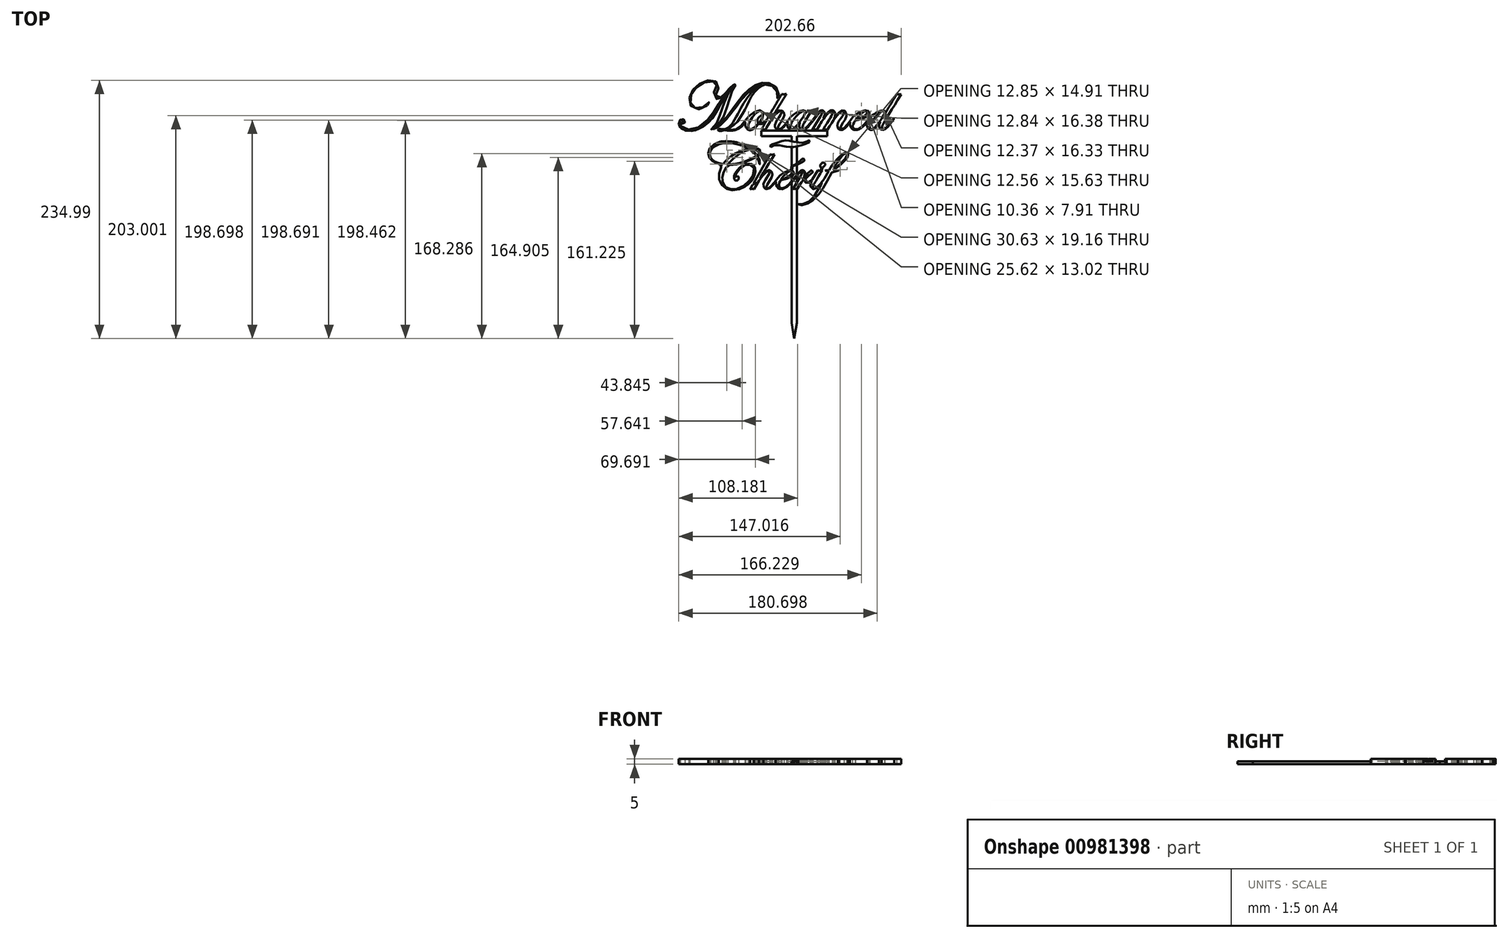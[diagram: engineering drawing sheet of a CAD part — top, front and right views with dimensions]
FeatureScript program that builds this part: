
annotation { "Feature Type Name" : "Feature", "Feature Type Description" : "" }
export const myFeature = defineFeature(function(context is Context, id is Id, definition is map)
    precondition{}
    {
        {
            var Q0;
            Q0=qCreatedBy(makeId("Top.planeOp"),FACE);
            var sketch = newSketch(context, id + "F0", { "sketchPlane" : qUnion([Q0])});
            skPoint(sketch, "E0", {"position": v(0, -6.46) * mm});
            skFitSpline(sketch, "E1", {"points": [v(-62.76, 39.27) * mm, v(-62.6, 39.54) * mm, v(-62.38, 39.63) * mm, v(-62.04, 39.52) * mm, v(-62, 38.94) * mm, v(-62.2, 38.46) * mm, v(-62.86, 37.49) * mm, v(-63.7, 36.53) * mm, v(-64.47, 35.77) * mm, v(-65.58, 34.8) * mm, v(-66.63, 34.03) * mm, v(-67.77, 33.57) * mm, v(-69, 33.44) * mm, v(-70.14, 33.54) * mm, v(-71.55, 34.27) * mm, v(-72.56, 35.4) * mm, v(-73.2, 36.81) * mm, v(-73.3, 38.17) * mm, v(-73.11, 39.6) * mm, v(-72.75, 40.63) * mm, v(-72.19, 41.92) * mm, v(-71.5, 43.34) * mm, v(-71.04, 44.4) * mm, v(-70.56, 45.74) * mm, v(-70.43, 46.6) * mm, v(-70.62, 47.57) * mm, v(-71.18, 48.46) * mm, v(-71.68, 48.93) * mm, v(-72.36, 49.32) * mm, v(-73.34, 49.67) * mm, v(-74.48, 49.91) * mm, v(-77.25, 49.95) * mm, v(-79.05, 49.67) * mm, v(-80.65, 49.25) * mm, v(-82.83, 48.34) * mm, v(-84.93, 47.23) * mm, v(-86.3, 46.3) * mm, v(-87.57, 45.33) * mm, v(-89.12, 43.96) * mm, v(-90.43, 42.65) * mm, v(-91.75, 41.08) * mm, v(-92.94, 39.15) * mm, v(-93.79, 37.48) * mm, v(-94.18, 36.2) * mm, v(-94.62, 34.55) * mm, v(-94.73, 33.03) * mm, v(-94.7, 31.33) * mm, v(-94.29, 29.7) * mm, v(-93.87, 28.77) * mm, v(-93.21, 27.84) * mm, v(-92.45, 26.95) * mm, v(-91.42, 26.19) * mm, v(-90.16, 25.63) * mm, v(-88.64, 25.3) * mm, v(-87.7, 25.27) * mm, v(-86.07, 25.4) * mm, v(-84.35, 25.84) * mm, v(-83.05, 26.37) * mm, v(-81.66, 27.15) * mm, v(-79.8, 28.44) * mm, v(-78.83, 29.35) * mm, v(-77.89, 30.4) * mm, v(-77.52, 30.98) * mm, v(-77.35, 31.17) * mm, v(-77.04, 31.24) * mm, v(-76.77, 31) * mm, v(-76.74, 30.42) * mm, v(-77.2, 29.8) * mm, v(-78.33, 28.66) * mm, v(-79.78, 27.44) * mm, v(-81.13, 26.47) * mm, v(-82.79, 25.55) * mm, v(-85.24, 24.7) * mm, v(-87.4, 24.46) * mm, v(-89.27, 24.57) * mm, v(-91.84, 25.48) * mm, v(-93.31, 26.58) * mm, v(-94.23, 27.62) * mm, v(-95, 28.9) * mm, v(-95.55, 30.89) * mm, v(-95.63, 32.2) * mm, v(-95.6, 33.98) * mm, v(-95.23, 35.93) * mm, v(-94.64, 37.86) * mm, v(-93.83, 39.46) * mm, v(-92.98, 40.93) * mm, v(-91.91, 42.4) * mm, v(-90.55, 43.9) * mm, v(-89.36, 45.03) * mm, v(-88.06, 46.14) * mm, v(-86.31, 47.4) * mm, v(-83.87, 48.82) * mm, v(-82.24, 49.54) * mm, v(-80.43, 50.12) * mm, v(-78.86, 50.5) * mm, v(-76.91, 50.72) * mm, v(-75.68, 50.77) * mm, v(-73.8, 50.66) * mm, v(-72.42, 50.28) * mm, v(-71.14, 49.63) * mm, v(-70.3, 48.91) * mm, v(-69.5, 47.8) * mm, v(-68.94, 46.44) * mm, v(-68.84, 44.6) * mm, v(-69.17, 42.94) * mm, v(-69.77, 41.1) * mm, v(-70.43, 39.66) * mm, v(-71, 38.32) * mm, v(-71.26, 37.62) * mm, v(-71.51, 36.56) * mm, v(-71.42, 35.54) * mm, v(-70.69, 34.74) * mm, v(-69.92, 34.4) * mm, v(-68.4, 34.37) * mm, v(-66.52, 35.2) * mm, v(-64.51, 36.88) * mm, v(-63.27, 38.48) * mm, v(-62.76, 39.27) * mm]});
            skFitSpline(sketch, "E2", {"points": [v(-104.1, 12.23) * mm, v(-104.04, 12.78) * mm, v(-103.88, 13.03) * mm, v(-103.68, 13.06) * mm, v(-103.53, 12.82) * mm, v(-103.51, 12.13) * mm, v(-103.41, 11.53) * mm, v(-103, 11.02) * mm, v(-102.14, 10.75) * mm, v(-101.11, 10.84) * mm, v(-100.18, 11.53) * mm, v(-99.66, 12.4) * mm, v(-99.52, 13.2) * mm, v(-99.6, 14.3) * mm, v(-100.24, 15.07) * mm, v(-101.15, 15.48) * mm, v(-102.26, 15.45) * mm, v(-103.07, 15.2) * mm, v(-103.62, 14.87) * mm, v(-104.24, 14.22) * mm, v(-104.8, 13.28) * mm, v(-105.02, 12.5) * mm, v(-105.16, 11.06) * mm, v(-104.76, 9.4) * mm, v(-104.06, 8.18) * mm, v(-102.92, 7.05) * mm, v(-101.64, 6.2) * mm, v(-100.35, 5.54) * mm, v(-98.95, 5.08) * mm, v(-97.71, 4.81) * mm, v(-95.52, 4.68) * mm, v(-93.28, 4.78) * mm, v(-90.97, 5.17) * mm, v(-88.23, 5.96) * mm, v(-85.63, 7.09) * mm, v(-83.84, 8.17) * mm, v(-81.5, 9.62) * mm, v(-79.45, 11.14) * mm, v(-78.05, 12.46) * mm, v(-76.34, 14.26) * mm, v(-75.31, 15.46) * mm, v(-73.29, 18.2) * mm, v(-71.17, 21.5) * mm, v(-69.94, 23.64) * mm, v(-68.77, 25.81) * mm, v(-67.45, 28.3) * mm, v(-66.25, 30.54) * mm, v(-65.24, 32.46) * mm, v(-64.39, 33.83) * mm, v(-63.74, 34.91) * mm, v(-61.65, 38.33) * mm, v(-60.27, 40.28) * mm, v(-58.56, 42.43) * mm, v(-57.54, 43.6) * mm, v(-56.65, 44.53) * mm, v(-55.73, 45.31) * mm, v(-55.47, 45.4) * mm, v(-55.9, 44.92) * mm, v(-56.63, 44.19) * mm, v(-57.73, 42.77) * mm, v(-58.66, 41.39) * mm, v(-59.5, 39.98) * mm, v(-60.38, 38.35) * mm, v(-61.43, 36.24) * mm, v(-62.16, 34.56) * mm, v(-62.9, 32.68) * mm, v(-64.37, 28.71) * mm, v(-65.1, 26.41) * mm, v(-67.48, 19.6) * mm, v(-67.94, 18.27) * mm, v(-68.34, 17.02) * mm, v(-68.94, 15.55) * mm, v(-69.85, 13.29) * mm, v(-70.55, 11.74) * mm, v(-71.24, 10.5) * mm, v(-72.42, 8.82) * mm, v(-73.72, 7.5) * mm, v(-74.86, 6.53) * mm, v(-75.6, 5.98) * mm, v(-75.99, 5.56) * mm, v(-75.66, 5.35) * mm, v(-74.58, 5.5) * mm, v(-72.84, 6.15) * mm, v(-71.4, 6.88) * mm, v(-69.46, 8.15) * mm, v(-67.86, 9.28) * mm, v(-66.16, 10.88) * mm, v(-62.54, 14.6) * mm, v(-57.85, 20.25) * mm, v(-54.53, 24.54) * mm, v(-48.39, 32.59) * mm, v(-46.3, 35.03) * mm, v(-44.15, 37.45) * mm, v(-41.9, 39.66) * mm, v(-40.15, 41.13) * mm, v(-38, 42.77) * mm, v(-36.35, 43.94) * mm, v(-34.71, 44.81) * mm, v(-32.96, 45.7) * mm, v(-31.49, 46.26) * mm, v(-29.49, 46.72) * mm, v(-27.83, 46.97) * mm, v(-25.56, 46.97) * mm, v(-23.7, 46.76) * mm, v(-22, 46.36) * mm, v(-20.3, 45.61) * mm, v(-18.65, 44.49) * mm, v(-17.22, 43.17) * mm, v(-16.1, 41.57) * mm, v(-15.4, 39.99) * mm, v(-15.07, 37.97) * mm, v(-15.1, 36.15) * mm, v(-15.4, 34.86) * mm, v(-15.56, 34.23) * mm, v(-15.34, 33.85) * mm, v(-14.82, 33.98) * mm, v(-14.52, 34.86) * mm, v(-14.17, 36.97) * mm, v(-14.3, 39.57) * mm, v(-15.1, 42.09) * mm, v(-15.93, 43.6) * mm, v(-17.45, 45.29) * mm, v(-19.53, 46.83) * mm, v(-20.68, 47.48) * mm, v(-23.27, 48.27) * mm, v(-24.66, 48.44) * mm, v(-26.15, 48.51) * mm, v(-27.8, 48.5) * mm, v(-29.22, 48.3) * mm, v(-31.25, 47.89) * mm, v(-33.64, 47.08) * mm, v(-35.38, 46.28) * mm, v(-36.97, 45.39) * mm, v(-38.48, 44.45) * mm, v(-40.35, 43.04) * mm, v(-41.41, 42.23) * mm, v(-43.69, 40.18) * mm, v(-45.56, 38.24) * mm, v(-46.75, 36.95) * mm, v(-49.15, 33.96) * mm, v(-50.8, 31.9) * mm, v(-52.5, 29.6) * mm, v(-53.49, 28.19) * mm, v(-55.27, 25.76) * mm, v(-57.05, 23.37) * mm, v(-59.03, 20.64) * mm, v(-60.43, 18.83) * mm, v(-63.08, 15.44) * mm, v(-65.51, 12.66) * mm, v(-66.88, 11.3) * mm, v(-68.94, 9.66) * mm, v(-71.06, 7.98) * mm, v(-72.8, 7.01) * mm, v(-73.58, 6.72) * mm, v(-71.93, 7.85) * mm, v(-70.57, 8.92) * mm, v(-68.96, 10.5) * mm, v(-67.4, 12.3) * mm, v(-66.06, 14.46) * mm, v(-65.1, 16.1) * mm, v(-63.36, 20.12) * mm, v(-62.63, 22.2) * mm, v(-61.07, 26.75) * mm, v(-60.4, 28.98) * mm, v(-59.35, 32.54) * mm, v(-58.7, 34.84) * mm, v(-57.69, 38.18) * mm, v(-56.82, 40.68) * mm, v(-55.97, 42.75) * mm, v(-55.12, 44.3) * mm, v(-54.29, 45.57) * mm, v(-53.7, 46.31) * mm, v(-53.58, 46.76) * mm, v(-53.87, 46.94) * mm, v(-54.62, 46.82) * mm, v(-55.46, 46.4) * mm, v(-56.39, 45.69) * mm, v(-57.57, 44.61) * mm, v(-58.95, 43.18) * mm, v(-60.16, 41.84) * mm, v(-61.62, 40) * mm, v(-62.7, 38.53) * mm, v(-63.62, 37.28) * mm, v(-66.11, 33.26) * mm, v(-68.3, 29.8) * mm, v(-70.88, 25.5) * mm, v(-74, 20.58) * mm, v(-76, 17.9) * mm, v(-78.55, 15.03) * mm, v(-81.03, 12.4) * mm, v(-83.53, 10.18) * mm, v(-86.75, 8.1) * mm, v(-88.75, 7.17) * mm, v(-91.29, 6.27) * mm, v(-93.65, 5.83) * mm, v(-95.92, 5.76) * mm, v(-98.1, 6.06) * mm, v(-100.25, 6.67) * mm, v(-101.85, 7.59) * mm, v(-103.04, 8.67) * mm, v(-103.93, 10.37) * mm, v(-104.1, 12.23) * mm]});
            skFitSpline(sketch, "E3", {"points": [v(-63.32, 5.52) * mm, v(-66.2, 4.77) * mm, v(-68.7, 4.84) * mm, v(-69.35, 5.3) * mm, v(-69.4, 5.82) * mm, v(-68.9, 6.32) * mm, v(-67.94, 6.54) * mm, v(-66.1, 6.52) * mm, v(-63.68, 6.27) * mm, v(-62.84, 6.32) * mm, v(-60.23, 7.8) * mm, v(-58.78, 8.88) * mm, v(-57.03, 10.78) * mm, v(-55.7, 12.64) * mm, v(-54.18, 15.1) * mm, v(-52.3, 18.5) * mm, v(-50.64, 21.58) * mm, v(-49, 24.67) * mm, v(-47.62, 27.12) * mm, v(-46.44, 29.09) * mm, v(-45.4, 30.83) * mm, v(-44.24, 32.7) * mm, v(-43.1, 34.35) * mm, v(-41.72, 36.3) * mm, v(-39.95, 38.46) * mm, v(-38, 40.5) * mm, v(-36.26, 42.08) * mm, v(-34.22, 43.79) * mm, v(-32.29, 45.03) * mm, v(-30.12, 46.32) * mm, v(-28.34, 47.09) * mm, v(-27.84, 47.24) * mm, v(-27.52, 47.28) * mm, v(-27.04, 47.35) * mm, v(-26.54, 47.2) * mm, v(-26.48, 46.92) * mm, v(-27.17, 46.74) * mm, v(-28.2, 46.4) * mm, v(-28.76, 46.13) * mm, v(-29.34, 45.78) * mm, v(-30, 45.37) * mm, v(-30.62, 45.06) * mm, v(-31.68, 44.34) * mm, v(-32.7, 43.6) * mm, v(-33.44, 43.04) * mm, v(-34.4, 42.08) * mm, v(-35.77, 40.67) * mm, v(-36.94, 39.15) * mm, v(-37.87, 37.68) * mm, v(-38.6, 36.5) * mm, v(-39.2, 35.42) * mm, v(-39.79, 34.5) * mm, v(-40.19, 33.77) * mm, v(-40.75, 32.7) * mm, v(-41.26, 31.67) * mm, v(-41.62, 31) * mm, v(-42.18, 29.78) * mm, v(-42.92, 28.27) * mm, v(-43.45, 27.13) * mm, v(-44.15, 25.75) * mm, v(-44.62, 24.83) * mm, v(-44.97, 24.09) * mm, v(-45.53, 23.05) * mm, v(-46.17, 21.85) * mm, v(-46.75, 20.78) * mm, v(-47.21, 19.95) * mm, v(-47.82, 18.93) * mm, v(-48.34, 18.04) * mm, v(-48.88, 17.13) * mm, v(-49.57, 16.14) * mm, v(-50.23, 15.23) * mm, v(-50.98, 14.15) * mm, v(-51.55, 13.43) * mm, v(-52.25, 12.58) * mm, v(-53.48, 11.3) * mm, v(-54.25, 10.55) * mm, v(-55.18, 9.76) * mm, v(-55.99, 9.09) * mm, v(-56.92, 8.44) * mm, v(-58.17, 7.68) * mm, v(-59.45, 6.97) * mm, v(-60.42, 6.48) * mm, v(-61.18, 6.2) * mm, v(-61.82, 5.97) * mm, v(-61.76, 5.87) * mm, v(-61.43, 5.86) * mm, v(-61.16, 5.82) * mm, v(-60.3, 5.74) * mm, v(-58.93, 5.64) * mm, v(-57.24, 5.68) * mm, v(-55.93, 5.81) * mm, v(-54.73, 6) * mm, v(-53.3, 6.36) * mm, v(-51.67, 6.97) * mm, v(-49.92, 8.03) * mm, v(-48.15, 9.83) * mm, v(-46.49, 11.62) * mm, v(-44.96, 13.52) * mm, v(-43.55, 15.23) * mm, v(-42.2, 16.92) * mm, v(-41.29, 17.9) * mm, v(-40, 19.03) * mm, v(-37.87, 20.7) * mm, v(-36.32, 21.7) * mm, v(-34.55, 22.63) * mm, v(-33.29, 23.08) * mm, v(-31.7, 23.43) * mm, v(-30.46, 23.43) * mm, v(-29.44, 23.19) * mm, v(-28.5, 22.42) * mm, v(-28.03, 20.64) * mm, v(-28.19, 19.02) * mm, v(-28.68, 17.2) * mm, v(-29.05, 16.3) * mm, v(-30.17, 14.18) * mm, v(-31.1, 12.8) * mm, v(-31.9, 11.8) * mm], "startDerivative": vector(-226.38, -73.79) * mm, "endDerivative": vector(-96.8, -119.92) * mm});
            skFitSpline(sketch, "E4", {"points": [v(-31.9, 11.8) * mm, v(-31.47, 11.66) * mm, v(-30.7, 11.57) * mm, v(-29.75, 11.67) * mm, v(-28.23, 12.3) * mm, v(-27.16, 13.03) * mm, v(-25.9, 14.1) * mm, v(-24.7, 15.46) * mm, v(-24.13, 16.4) * mm, v(-23.54, 17.52) * mm, v(-22.98, 18.48) * mm, v(-22.43, 19.48) * mm], "startDerivative": vector(6.79, -2.6) * mm, "endDerivative": vector(6.08, 11.27) * mm});
            skFitSpline(sketch, "E5", {"points": [v(-22.43, 19.48) * mm, v(-21.36, 21.31) * mm, v(-20.4, 22.93) * mm, v(-19.52, 24.34) * mm, v(-18.1, 26.8) * mm, v(-17.02, 28.68) * mm, v(-15.7, 30.88) * mm, v(-15.2, 31.72) * mm, v(-13.65, 34.35) * mm, v(-13.2, 35.13) * mm, v(-12.36, 36.53) * mm, v(-11.9, 37.3) * mm, v(-11.26, 38.29) * mm], "startDerivative": vector(11.81, 20.1) * mm, "endDerivative": vector(10.2, 15.26) * mm});
            skFitSpline(sketch, "E6", {"points": [v(-11.26, 38.29) * mm, v(-10.67, 38.12) * mm, v(-9.9, 38.03) * mm, v(-8.89, 38.09) * mm, v(-8, 38.26) * mm, v(-7.1, 38.43) * mm], "startDerivative": vector(3.35, -1.1) * mm, "endDerivative": vector(4.37, 0.78) * mm});
            skFitSpline(sketch, "E7", {"points": [v(-7.1, 38.43) * mm, v(-7.44, 37.63) * mm, v(-8.1, 36.6) * mm, v(-8.92, 35.3) * mm, v(-9.6, 34.17) * mm, v(-10.49, 32.76) * mm, v(-11.34, 31.36) * mm, v(-12.43, 29.63) * mm, v(-13.38, 28.14) * mm, v(-14.27, 26.65) * mm, v(-15.73, 24.38) * mm, v(-17.3, 21.75) * mm, v(-18.56, 19.73) * mm, v(-19.17, 18.74) * mm, v(-19.9, 17.58) * mm, v(-21.04, 15.8) * mm], "startDerivative": vector(-6.48, -16.6) * mm, "endDerivative": vector(-16.06, -25.3) * mm});
            skFitSpline(sketch, "E8", {"points": [v(-21.04, 15.8) * mm, v(-18.36, 19.32) * mm, v(-17.41, 20.38) * mm, v(-16.07, 21.7) * mm, v(-14.6, 22.74) * mm, v(-13.55, 23.26) * mm, v(-12.65, 23.4) * mm, v(-11.95, 23.34) * mm, v(-10.76, 22.9) * mm, v(-10.02, 22.09) * mm, v(-9.52, 21.36) * mm, v(-9.21, 20.47) * mm, v(-9.1, 19.25) * mm, v(-9.12, 18.51) * mm, v(-9.49, 17.44) * mm, v(-10.14, 15.99) * mm, v(-10.81, 14.7) * mm, v(-11.79, 13.24) * mm, v(-12.6, 11.98) * mm, v(-13.14, 11.18) * mm, v(-13.7, 10.2) * mm, v(-14.4, 9.01) * mm, v(-14.85, 8.02) * mm, v(-14.97, 7.4) * mm, v(-14.9, 6.92) * mm, v(-14.62, 6.52) * mm, v(-14.16, 6.28) * mm, v(-13.77, 6.22) * mm, v(-13.27, 6.26) * mm, v(-12.64, 6.58) * mm, v(-11.64, 7.27) * mm, v(-10.4, 8.35) * mm, v(-8.9, 10.02) * mm, v(-7.64, 11.56) * mm, v(-6.53, 13.01) * mm, v(-5.44, 14.45) * mm, v(-4.64, 15.68) * mm, v(-3.7, 16.85) * mm, v(-2.77, 17.87) * mm, v(-1.7, 18.82) * mm, v(0.13, 20.1) * mm, v(1.71, 21.07) * mm, v(3.69, 22.1) * mm, v(5.9, 23.02) * mm, v(7.26, 23.32) * mm, v(8.27, 23.41) * mm, v(9, 23.37) * mm, v(9.8, 23) * mm, v(10.2, 22.5) * mm, v(10.34, 21.54) * mm, v(10.22, 20.53) * mm], "startDerivative": vector(80.75, 108.83) * mm, "endDerivative": vector(-9.77, -54.96) * mm});
            skFitSpline(sketch, "E9", {"points": [v(10.22, 20.53) * mm, v(11.54, 23.23) * mm], "startDerivative": vector(1.32, 2.7) * mm, "endDerivative": vector(1.32, 2.7) * mm});
            skFitSpline(sketch, "E10", {"points": [v(11.54, 23.23) * mm, v(12.61, 22.99) * mm, v(13.89, 22.94) * mm, v(15.2, 23.13) * mm, v(15.66, 23.23) * mm], "startDerivative": vector(4.04, -1.07) * mm, "endDerivative": vector(2.28, 0.55) * mm});
            skFitSpline(sketch, "E11", {"points": [v(15.66, 23.23) * mm, v(10.54, 14.73) * mm, v(8.84, 11.8) * mm, v(7.99, 10.1) * mm, v(7.41, 8.81) * mm, v(7.14, 7.7) * mm, v(7.22, 6.93) * mm, v(7.6, 6.39) * mm, v(8.26, 6.17) * mm, v(8.96, 6.4) * mm, v(10.1, 7.1) * mm, v(11.54, 8.33) * mm, v(12.8, 9.7) * mm, v(14.4, 11.54) * mm, v(16.4, 14.14) * mm, v(19.12, 17.77) * mm, v(21.84, 21.16) * mm, v(23.21, 22.42) * mm, v(24.17, 23.11) * mm, v(24.91, 23.34) * mm, v(25.41, 23.37) * mm, v(26.06, 23.23) * mm, v(26.68, 22.75) * mm, v(27.26, 22.03) * mm, v(27.58, 21.16) * mm, v(27.68, 19.72) * mm, v(27.5, 18.75) * mm, v(27.1, 17.5) * mm, v(26.56, 16.41) * mm], "startDerivative": vector(-65.23, -108.07) * mm, "endDerivative": vector(-18.62, -33.73) * mm});
            skFitSpline(sketch, "E12", {"points": [v(26.56, 16.41) * mm, v(28.85, 19.48) * mm, v(30.36, 21.14) * mm, v(31.88, 22.56) * mm, v(32.93, 23.17) * mm, v(34, 23.47) * mm, v(34.57, 23.44) * mm, v(35, 23.31) * mm, v(35.64, 23) * mm, v(36.2, 22.53) * mm, v(36.59, 22.01) * mm, v(36.9, 21.41) * mm, v(37.21, 20.46) * mm, v(37.24, 19.54) * mm, v(37.19, 18.78) * mm, v(36.9, 17.76) * mm, v(36.57, 17) * mm, v(36.38, 16.64) * mm, v(35.97, 15.93) * mm], "startDerivative": vector(22.24, 30.87) * mm, "endDerivative": vector(-9.01, -15.88) * mm});
            skFitSpline(sketch, "E13", {"points": [v(35.97, 15.93) * mm, v(36.82, 17.06) * mm, v(37.6, 18.08) * mm, v(39.05, 19.83) * mm, v(39.96, 20.74) * mm, v(40.85, 21.59) * mm, v(41.7, 22.3) * mm, v(42.6, 22.9) * mm, v(43.55, 23.33) * mm, v(44.26, 23.45) * mm, v(45.03, 23.37) * mm, v(45.86, 23) * mm, v(46.26, 22.72) * mm, v(46.7, 22.26) * mm, v(47.05, 21.73) * mm, v(47.4, 20.94) * mm, v(47.6, 20.08) * mm, v(47.66, 18.94) * mm, v(47.56, 18.15) * mm, v(47.17, 16.86) * mm, v(46.6, 15.56) * mm, v(45.96, 14.48) * mm, v(45.4, 13.66) * mm, v(44.74, 12.7) * mm, v(43.72, 11.2) * mm, v(42.76, 9.7) * mm, v(42.12, 8.38) * mm, v(41.94, 7.4) * mm, v(42.07, 6.72) * mm, v(42.5, 6.32) * mm, v(43, 6.2) * mm, v(43.97, 6.39) * mm, v(45.43, 7.39) * mm, v(46.87, 8.84) * mm, v(48.7, 10.9) * mm, v(50.37, 13.12) * mm, v(51.63, 14.79) * mm, v(51.99, 15.46) * mm, v(53.4, 17.3) * mm, v(54.66, 18.5) * mm, v(57, 20.22) * mm, v(59.17, 21.44) * mm, v(60.84, 22.29) * mm, v(62.37, 22.89) * mm, v(64, 23.32) * mm, v(65.06, 23.44) * mm, v(66.04, 23.34) * mm, v(67, 22.97) * mm, v(67.58, 22.51) * mm, v(68, 21.93) * mm, v(68.23, 21.06) * mm, v(68.12, 20.02) * mm, v(67.6, 18.97) * mm, v(66.85, 18.2) * mm, v(65.47, 17.2) * mm, v(64.43, 16.66) * mm, v(62.97, 16.06) * mm, v(61.16, 15.45) * mm, v(59.33, 14.96) * mm, v(57.58, 14.53) * mm, v(56.16, 14.23) * mm, v(55.4, 14.1) * mm], "startDerivative": vector(50.94, 68.1) * mm, "endDerivative": vector(-55.23, -9.52) * mm});
            skFitSpline(sketch, "E14", {"points": [v(55.91, 14.87) * mm, v(57.46, 16.93) * mm, v(58.45, 18.06) * mm, v(60.25, 19.86) * mm, v(61.8, 21.2) * mm, v(63.51, 22.28) * mm, v(64.8, 22.7) * mm, v(65.3, 22.74) * mm, v(65.75, 22.7) * mm, v(66, 22.54) * mm, v(66.14, 22.35) * mm, v(66.23, 22.11) * mm, v(66.26, 21.75) * mm, v(66.13, 21.22) * mm, v(65.85, 20.61) * mm, v(65.31, 19.87) * mm, v(64.48, 19) * mm, v(63.86, 18.5) * mm, v(62.89, 17.82) * mm, v(61.56, 17.03) * mm, v(60.34, 16.41) * mm, v(59.28, 15.98) * mm, v(58.2, 15.56) * mm, v(56.87, 15.12) * mm, v(56.13, 14.9) * mm], "startDerivative": vector(24.92, 34) * mm, "endDerivative": vector(-18.62, -5.6) * mm});
            skLineSegment(sketch, "E15", {"start": v(56.13, 14.9) * mm, "end": v(55.89, 14.83) * mm});
            skLineSegment(sketch, "E16", {"start": v(55.89, 14.83) * mm, "end": v(55.91, 14.87) * mm});
            skFitSpline(sketch, "E17", {"points": [v(55.4, 14.1) * mm, v(54.5, 12.55) * mm, v(53.8, 11.05) * mm, v(53.52, 10.15) * mm, v(53.34, 8.86) * mm, v(53.46, 7.97) * mm, v(53.84, 7.13) * mm, v(54.73, 6.5) * mm, v(55.79, 6.29) * mm, v(57.03, 6.34) * mm, v(58.73, 6.87) * mm, v(60.3, 7.77) * mm, v(62.03, 9.06) * mm, v(63.07, 9.99) * mm, v(65.78, 12.97) * mm, v(67.24, 14.7) * mm, v(68.42, 16.26) * mm, v(69.25, 17.23) * mm, v(70.65, 18.53) * mm, v(72.06, 19.61) * mm, v(73.72, 20.7) * mm, v(75.22, 21.56) * mm, v(77.15, 22.53) * mm, v(78.93, 23.16) * mm, v(80.73, 23.44) * mm, v(81.81, 23.26) * mm, v(82.54, 22.72) * mm, v(82.86, 21.82) * mm, v(82.77, 20.74) * mm, v(82.49, 20.05) * mm], "startDerivative": vector(-24.88, -40.4) * mm, "endDerivative": vector(-13.28, -26.18) * mm});
            skFitSpline(sketch, "E18", {"points": [v(82.49, 20.05) * mm, v(84.14, 22.87) * mm, v(86.37, 26.76) * mm, v(87.98, 29.35) * mm, v(89.95, 32.64) * mm, v(91.24, 34.84) * mm, v(93.3, 38.26) * mm], "startDerivative": vector(9.7, 16.4) * mm, "endDerivative": vector(12.45, 20.61) * mm});
            skFitSpline(sketch, "E19", {"points": [v(93.3, 38.26) * mm, v(93.92, 38.1) * mm, v(94.92, 37.9) * mm, v(96.11, 37.91) * mm, v(97.5, 38.1) * mm], "startDerivative": vector(3, -0.71) * mm, "endDerivative": vector(4.41, 0.64) * mm});
            skFitSpline(sketch, "E20", {"points": [v(97.5, 38.1) * mm, v(93.97, 32.48) * mm, v(92.6, 30.28) * mm, v(90.43, 26.74) * mm, v(88.7, 23.97) * mm, v(86.24, 19.97) * mm, v(84.77, 17.56) * mm, v(83.26, 15.14) * mm, v(81.73, 12.49) * mm, v(80.79, 10.64) * mm, v(79.88, 8.77) * mm, v(79.64, 7.97) * mm, v(79.6, 7.38) * mm, v(79.71, 6.8) * mm, v(80.03, 6.45) * mm, v(80.53, 6.22) * mm, v(80.96, 6.2) * mm, v(81.71, 6.46) * mm, v(82.92, 7.22) * mm, v(84.12, 8.27) * mm, v(84.81, 8.94) * mm, v(86.15, 10.5) * mm, v(87.22, 11.82) * mm, v(88.64, 13.73) * mm, v(89.42, 14.81) * mm, v(90.33, 16.14) * mm, v(90.54, 16.4) * mm, v(90.79, 16.46) * mm, v(90.97, 16.4) * mm, v(91.05, 16.15) * mm, v(90.93, 15.82) * mm, v(90.58, 15.3) * mm, v(90.15, 14.73) * mm, v(89.4, 13.64) * mm, v(88.6, 12.63) * mm, v(87.4, 11.08) * mm, v(86.51, 9.97) * mm, v(85.05, 8.31) * mm, v(84.26, 7.55) * mm, v(83.3, 6.74) * mm, v(82.42, 6.11) * mm, v(81.6, 5.66) * mm, v(80.82, 5.47) * mm, v(80.06, 5.5) * mm, v(79.32, 5.68) * mm, v(78.51, 6.14) * mm, v(77.89, 6.84) * mm, v(77.42, 7.78) * mm, v(77.27, 8.65) * mm, v(77.18, 9.4) * mm, v(77.3, 10.64) * mm, v(77.58, 11.55) * mm, v(77.88, 12.33) * mm, v(78.2, 12.94) * mm], "startDerivative": vector(-93.17, -148.36) * mm, "endDerivative": vector(23.9, 42.1) * mm});
            skFitSpline(sketch, "E21", {"points": [v(78.2, 12.94) * mm, v(76.97, 11.17) * mm, v(76, 9.94) * mm, v(75.15, 8.97) * mm, v(74.13, 7.82) * mm, v(73.42, 7.15) * mm, v(72.44, 6.38) * mm, v(71.58, 5.81) * mm, v(70.7, 5.5) * mm, v(69.74, 5.54) * mm, v(68.63, 5.87) * mm, v(67.67, 6.66) * mm, v(66.9, 7.76) * mm, v(66.45, 8.9) * mm, v(66.31, 9.94) * mm, v(66.26, 10.93) * mm, v(66.4, 11.96) * mm, v(66.57, 12.65) * mm, v(66.75, 13.1) * mm], "startDerivative": vector(-16.26, -24.11) * mm, "endDerivative": vector(4.86, 11.86) * mm});
            skFitSpline(sketch, "E22", {"points": [v(66.75, 13.1) * mm, v(65.97, 12.1) * mm, v(64.93, 10.9) * mm, v(64, 9.97) * mm, v(62.33, 8.48) * mm, v(61.06, 7.48) * mm, v(59.93, 6.71) * mm, v(58.86, 6.12) * mm, v(57.19, 5.58) * mm, v(55.99, 5.47) * mm, v(54.62, 5.62) * mm, v(53.09, 6.3) * mm, v(51.87, 7.51) * mm, v(51.05, 8.88) * mm, v(50.74, 10.63) * mm, v(50.93, 12.87) * mm], "startDerivative": vector(-12.17, -16.23) * mm, "endDerivative": vector(3.84, 28.84) * mm});
            skFitSpline(sketch, "E23", {"points": [v(50.93, 12.87) * mm, v(49.87, 11.38) * mm, v(48.46, 9.62) * mm, v(47.26, 8.27) * mm, v(45.89, 7.02) * mm, v(44.74, 6.16) * mm, v(43.5, 5.53) * mm, v(42.49, 5.46) * mm, v(41.43, 5.76) * mm, v(40.52, 6.4) * mm, v(39.8, 7.36) * mm, v(39.5, 8.29) * mm, v(39.39, 8.88) * mm, v(39.33, 9.48) * mm, v(39.43, 10.6) * mm, v(39.9, 12.08) * mm, v(41, 14.1) * mm, v(42.02, 15.56) * mm, v(42.95, 16.93) * mm, v(44.26, 18.84) * mm, v(44.98, 20.18) * mm, v(45.34, 21.13) * mm, v(45.46, 21.7) * mm, v(45.2, 22.32) * mm, v(44.61, 22.7) * mm, v(44.14, 22.68) * mm, v(43.36, 22.5) * mm, v(42.38, 21.95) * mm, v(41.28, 21.11) * mm, v(39.9, 19.83) * mm, v(38.82, 18.55) * mm, v(37.12, 16.37) * mm, v(35.81, 14.63) * mm, v(34.29, 12.33) * mm, v(32.55, 9.64) * mm, v(30.18, 5.76) * mm], "startDerivative": vector(-31.63, -45.6) * mm, "endDerivative": vector(-49.03, -81.01) * mm});
            skFitSpline(sketch, "E24", {"points": [v(30.18, 5.76) * mm, v(29.03, 5.94) * mm, v(27.67, 5.94) * mm, v(26.83, 5.88) * mm, v(26.1, 5.76) * mm], "startDerivative": vector(-3.94, 0.88) * mm, "endDerivative": vector(-3.25, -0.54) * mm});
            skFitSpline(sketch, "E25", {"points": [v(26.1, 5.76) * mm, v(31.2, 13.98) * mm, v(33.36, 17.63) * mm, v(34.44, 19.92) * mm, v(34.9, 21.36) * mm, v(34.77, 22.18) * mm, v(34.23, 22.7) * mm, v(33.49, 22.64) * mm, v(32.46, 22.1) * mm, v(31.44, 21.23) * mm, v(30.4, 20.18) * mm, v(28.99, 18.65) * mm, v(27.95, 17.36) * mm, v(26.36, 15.24) * mm, v(25.2, 13.54) * mm, v(24.04, 11.81) * mm, v(23.13, 10.32) * mm, v(21.7, 7.84) * mm, v(20.52, 5.76) * mm], "startDerivative": vector(46.38, 74.9) * mm, "endDerivative": vector(-18.68, -33.21) * mm});
            skFitSpline(sketch, "E26", {"points": [v(20.52, 5.76) * mm, v(19.18, 5.94) * mm, v(17.83, 5.92) * mm, v(16.32, 5.76) * mm], "startDerivative": vector(-4.12, 0.68) * mm, "endDerivative": vector(-4.42, -0.53) * mm});
            skFitSpline(sketch, "E27", {"points": [v(16.32, 5.76) * mm, v(23.07, 16.49) * mm, v(24.92, 19.92) * mm, v(25.34, 21.03) * mm, v(25.5, 21.8) * mm, v(25.47, 22.18) * mm, v(25.29, 22.52) * mm, v(25.17, 22.65) * mm, v(24.89, 22.7) * mm, v(24.6, 22.68) * mm, v(24.17, 22.42) * mm, v(23.3, 21.73) * mm, v(22.38, 20.8) * mm, v(13.78, 9.8) * mm, v(12.15, 7.97) * mm, v(11.18, 7.07) * mm, v(9.99, 6.15) * mm, v(8.88, 5.6) * mm, v(7.92, 5.47) * mm, v(6.9, 5.66) * mm, v(6.01, 6.16) * mm, v(5.17, 7.1) * mm, v(4.76, 8.12) * mm, v(4.62, 9.28) * mm, v(4.79, 10.44) * mm, v(5, 11.49) * mm, v(5.34, 12.32) * mm, v(5.55, 12.75) * mm], "startDerivative": vector(69.27, 107.63) * mm, "endDerivative": vector(8.93, 18.09) * mm});
            skFitSpline(sketch, "E28", {"points": [v(5.55, 12.75) * mm, v(3.66, 10.03) * mm, v(2.22, 8.25) * mm, v(1.22, 7.23) * mm, v(0.25, 6.43) * mm, v(-0.72, 5.81) * mm, v(-1.76, 5.54) * mm, v(-2.6, 5.47) * mm, v(-3.36, 5.67) * mm, v(-4.13, 6) * mm, v(-4.78, 6.54) * mm, v(-5.4, 7.31) * mm, v(-5.88, 8.3) * mm, v(-6.24, 9.56) * mm, v(-6.28, 10.9) * mm, v(-6.17, 11.82) * mm, v(-5.99, 12.51) * mm, v(-5.86, 12.92) * mm], "startDerivative": vector(-19.18, -28.43) * mm, "endDerivative": vector(3.31, 10.57) * mm});
            skFitSpline(sketch, "E29", {"points": [v(-5.86, 12.92) * mm, v(-7.81, 10.3) * mm, v(-9.09, 8.83) * mm, v(-10.6, 7.3) * mm, v(-11.64, 6.47) * mm, v(-12.79, 5.76) * mm, v(-13.69, 5.5) * mm, v(-14.62, 5.47) * mm, v(-15.34, 5.67) * mm, v(-16.05, 6.1) * mm, v(-16.9, 7) * mm, v(-17.45, 8.14) * mm, v(-17.62, 9.1) * mm, v(-17.61, 10.05) * mm, v(-17.17, 11.57) * mm, v(-16.2, 13.64) * mm, v(-15.51, 14.68) * mm, v(-14.9, 15.59) * mm, v(-13.04, 18.5) * mm, v(-12.25, 19.84) * mm, v(-11.53, 21.3) * mm, v(-11.47, 21.72) * mm, v(-11.72, 22.33) * mm, v(-12.24, 22.64) * mm, v(-12.78, 22.67) * mm, v(-13.37, 22.55) * mm, v(-14.64, 21.87) * mm, v(-15.78, 20.9) * mm, v(-17, 19.76) * mm, v(-17.73, 18.96) * mm, v(-19.14, 17.17) * mm, v(-20.21, 15.67) * mm, v(-21.87, 13.1) * mm, v(-22.85, 11.56) * mm, v(-24.5, 8.8) * mm, v(-25.47, 7.03) * mm, v(-26.27, 5.66) * mm], "startDerivative": vector(-49.26, -67.97) * mm, "endDerivative": vector(-27.25, -46.62) * mm});
            skFitSpline(sketch, "E30", {"points": [v(-26.27, 5.66) * mm, v(-27.46, 5.82) * mm, v(-28.37, 5.84) * mm, v(-29.2, 5.73) * mm, v(-29.98, 5.62) * mm], "startDerivative": vector(-4.34, 0.65) * mm, "endDerivative": vector(-3.36, -0.48) * mm});
            skFitSpline(sketch, "E31", {"points": [v(-29.98, 5.62) * mm, v(-28.07, 9.1) * mm, v(-25.91, 13.02) * mm, v(-25.4, 13.77) * mm, v(-25.33, 13.92) * mm], "startDerivative": vector(4.96, 8.93) * mm, "endDerivative": vector(0.75, 1.82) * mm});
            skFitSpline(sketch, "E32", {"points": [v(-25.33, 13.92) * mm, v(-26.14, 13.1) * mm, v(-27.54, 11.94) * mm, v(-28.77, 11.31) * mm, v(-30.09, 10.93) * mm, v(-31.57, 11.01) * mm, v(-32.22, 11.3) * mm], "startDerivative": vector(-4.68, -4.96) * mm, "endDerivative": vector(-4.57, 2.68) * mm});
            skFitSpline(sketch, "E33", {"points": [v(-32.22, 11.3) * mm, v(-32.96, 10.36) * mm, v(-33.9, 9.2) * mm, v(-35.12, 7.9) * mm, v(-36.13, 7.03) * mm, v(-37.67, 6.06) * mm, v(-39.21, 5.49) * mm, v(-40.26, 5.42) * mm, v(-41.48, 5.6) * mm, v(-42.4, 6.24) * mm, v(-43.21, 6.92) * mm, v(-43.92, 7.97) * mm, v(-44.52, 9.15) * mm, v(-44.65, 10.06) * mm, v(-44.68, 10.88) * mm, v(-44.61, 11.71) * mm, v(-44.42, 12.56) * mm, v(-44.26, 13.03) * mm], "startDerivative": vector(-12.02, -15.64) * mm, "endDerivative": vector(4.12, 11.25) * mm});
            skFitSpline(sketch, "E34", {"points": [v(-44.26, 13.03) * mm, v(-46, 10.88) * mm, v(-47.3, 9.42) * mm, v(-48.46, 8.37) * mm, v(-49.7, 7.28) * mm, v(-51.44, 6.26) * mm, v(-52.64, 5.76) * mm, v(-54.13, 5.32) * mm, v(-56.45, 5) * mm, v(-59.5, 4.98) * mm, v(-62.28, 5.32) * mm, v(-63.32, 5.52) * mm], "startDerivative": vector(-16.68, -20.68) * mm, "endDerivative": vector(-13.5, 2.93) * mm});
            skFitSpline(sketch, "E35", {"points": [v(-29.2, 17.94) * mm, v(-29.5, 18.48) * mm, v(-29.98, 18.65) * mm, v(-30.72, 18.44) * mm, v(-31.8, 17.6) * mm, v(-32.47, 16.8) * mm, v(-32.96, 16) * mm, v(-33.38, 15.1) * mm, v(-33.63, 13.92) * mm, v(-33.6, 13.35) * mm, v(-33.3, 12.52) * mm, v(-32.96, 12.03) * mm, v(-32.7, 11.7) * mm], "startDerivative": vector(-3.6, 8.44) * mm, "endDerivative": vector(4.24, -5.31) * mm});
            skFitSpline(sketch, "E36", {"points": [v(-29.2, 17.94) * mm, v(-29.04, 18.71) * mm, v(-28.9, 19.75) * mm, v(-28.87, 20.98) * mm, v(-29.28, 21.92) * mm, v(-29.91, 22.52) * mm, v(-30.94, 22.73) * mm, v(-31.8, 22.65) * mm, v(-32.55, 22.35) * mm, v(-33.33, 21.87) * mm, v(-33.85, 21.57) * mm, v(-34.77, 20.86) * mm, v(-35.57, 20.07) * mm, v(-36.34, 19.22) * mm, v(-37.9, 17.27) * mm, v(-38.99, 15.71) * mm, v(-40, 14.15) * mm, v(-40.46, 13.26) * mm, v(-41.14, 11.78) * mm, v(-41.68, 10.08) * mm, v(-41.85, 9.13) * mm, v(-41.86, 8.3) * mm, v(-41.76, 7.44) * mm, v(-41.38, 6.76) * mm, v(-40.77, 6.41) * mm, v(-40.02, 6.32) * mm, v(-39.04, 6.41) * mm, v(-37.76, 6.88) * mm, v(-36.42, 7.68) * mm, v(-35.18, 8.8) * mm, v(-34.04, 10.05) * mm, v(-32.7, 11.7) * mm], "startDerivative": vector(5.73, 28.27) * mm, "endDerivative": vector(31.35, 39.53) * mm});
            skFitSpline(sketch, "E37", {"points": [v(9.44, 20.04) * mm, v(8.9, 18.8) * mm, v(8.21, 17.58) * mm, v(7, 15.64) * mm, v(6.02, 14.24) * mm, v(4.6, 12.36) * mm, v(3.43, 10.86) * mm, v(2.2, 9.43) * mm, v(0.14, 7.36) * mm, v(-0.67, 6.77) * mm, v(-1.4, 6.39) * mm, v(-2.22, 6.27) * mm, v(-3, 6.43) * mm, v(-3.53, 7.17) * mm, v(-3.7, 8.14) * mm, v(-3.47, 9.53) * mm, v(-3.05, 10.89) * mm, v(-2.3, 12.5) * mm, v(-1.34, 14.02) * mm, v(-0.64, 15.01) * mm, v(1.02, 17.21) * mm, v(2.38, 18.74) * mm, v(3.63, 19.94) * mm, v(5.05, 21.24) * mm, v(6.46, 22.16) * mm, v(7.55, 22.57) * mm, v(8.32, 22.66) * mm, v(8.93, 22.59) * mm, v(9.37, 22.3) * mm, v(9.56, 21.72) * mm, v(9.58, 20.95) * mm, v(9.48, 20.21) * mm, v(9.44, 20.04) * mm]});
            skLineSegment(sketch, "E38", {"start": v(-70.91, 7.63) * mm, "end": v(-68.55, 5.63) * mm});
            skLineSegment(sketch, "E39", {"start": v(-68.55, 5.63) * mm, "end": v(-67, 6.25) * mm});
            skLineSegment(sketch, "E40", {"start": v(-67, 6.25) * mm, "end": v(-68.91, 9.14) * mm});
            skLineSegment(sketch, "E41", {"start": v(-68.91, 9.14) * mm, "end": v(-70.91, 7.63) * mm});
            skFitSpline(sketch, "E42", {"points": [v(78.66, 14.49) * mm, v(76.14, 11.02) * mm, v(74, 8.6) * mm, v(72.48, 7.18) * mm, v(71.04, 6.4) * mm, v(70.37, 6.26) * mm, v(69.63, 6.4) * mm, v(69.02, 7.12) * mm, v(68.87, 8.5) * mm, v(69.25, 10.28) * mm, v(70.23, 12.68) * mm, v(71.53, 14.68) * mm, v(73.46, 17.24) * mm, v(74.98, 18.94) * mm, v(77.13, 20.94) * mm, v(78.53, 21.95) * mm, v(79.89, 22.57) * mm, v(80.79, 22.68) * mm, v(81.36, 22.6) * mm, v(81.86, 22.22) * mm, v(82.07, 21.6) * mm, v(82.1, 20.8) * mm, v(81.89, 19.9) * mm, v(81.02, 18.14) * mm, v(80.2, 16.76) * mm, v(78.66, 14.49) * mm]});
            skFitSpline(sketch, "E43", {"points": [v(-21.19, -9.98) * mm, v(-19.1, -8.95) * mm, v(-16.88, -8.38) * mm, v(-14.6, -8.26) * mm, v(-13.03, -8.45) * mm, v(-9.63, -9.06) * mm, v(-6.77, -9.71) * mm, v(-2.92, -9.87) * mm, v(0.55, -9.79) * mm, v(4.44, -8.84) * mm, v(9.4, -7.3) * mm, v(13.68, -5.7) * mm, v(14.29, -4.56) * mm, v(13.37, -4) * mm, v(11.96, -4.72) * mm, v(7.65, -6.01) * mm, v(3.83, -5.9) * mm, v(-3.07, -4.41) * mm, v(-6.54, -3.92) * mm, v(-9.7, -4.3) * mm, v(-15.89, -6.05) * mm, v(-20.46, -7.96) * mm, v(-22, -9.14) * mm, v(-21.95, -9.79) * mm, v(-21.19, -9.98) * mm]});
            skFitSpline(sketch, "E44", {"points": [v(-53.65, -37.35) * mm, v(-52.93, -36.81) * mm, v(-52.37, -36.56) * mm, v(-51.83, -36.54) * mm, v(-51.34, -36.65) * mm, v(-50.79, -36.97) * mm, v(-50.46, -37.7) * mm, v(-50.41, -38.73) * mm, v(-50.68, -39.68) * mm, v(-51.37, -40.39) * mm, v(-52.49, -40.67) * mm, v(-53.6, -40.55) * mm, v(-54.3, -40) * mm, v(-54.7, -39.12) * mm, v(-54.82, -38.08) * mm, v(-54.69, -36.58) * mm, v(-54.35, -35.27) * mm, v(-53.57, -33.48) * mm, v(-52.4, -31.74) * mm, v(-50.48, -29.54) * mm, v(-48.73, -28) * mm, v(-47.01, -26.8) * mm, v(-44.25, -25.6) * mm, v(-42.5, -25.23) * mm, v(-40.89, -25.16) * mm, v(-39.2, -25.4) * mm, v(-37.79, -26.08) * mm, v(-36.74, -27.05) * mm, v(-35.98, -28.37) * mm, v(-35.66, -29.57) * mm, v(-35.5, -31.57) * mm, v(-35.56, -33.21) * mm, v(-35.89, -34.84) * mm, v(-36.48, -36.72) * mm, v(-37.15, -38.17) * mm, v(-38.2, -39.85) * mm, v(-39.33, -41.22) * mm, v(-40.69, -42.7) * mm, v(-41.62, -43.57) * mm, v(-43.09, -44.77) * mm, v(-44.57, -45.82) * mm, v(-45.85, -46.6) * mm, v(-47.12, -47.28) * mm, v(-48.91, -48) * mm, v(-50.33, -48.48) * mm, v(-52.64, -49.02) * mm, v(-55.63, -49.23) * mm, v(-57.53, -49.2) * mm, v(-58.99, -49) * mm, v(-60.38, -48.57) * mm, v(-62.16, -47.8) * mm, v(-63.4, -46.94) * mm, v(-64.72, -45.89) * mm, v(-66.55, -43.78) * mm, v(-67.51, -42.13) * mm, v(-68.19, -40.5) * mm, v(-68.62, -38.3) * mm, v(-68.73, -37.01) * mm, v(-68.64, -35.11) * mm, v(-68.43, -33.58) * mm, v(-67.93, -31.82) * mm, v(-67.12, -29.61) * mm, v(-65.97, -27.39) * mm, v(-65.08, -26.13) * mm, v(-65.08, -26.1) * mm, v(-65.15, -26.08) * mm, v(-66.93, -25.77) * mm, v(-68.7, -25.28) * mm, v(-70.6, -24.67) * mm, v(-72.5, -23.82) * mm, v(-74.35, -22.76) * mm, v(-75.3, -22.03) * mm, v(-76.63, -20.62) * mm, v(-77.4, -19.33) * mm, v(-77.9, -18.2) * mm, v(-78.16, -16.8) * mm, v(-78.17, -14.86) * mm, v(-77.98, -13.94) * mm, v(-77.58, -12.55) * mm, v(-77.03, -11.41) * mm, v(-76.18, -10.22) * mm, v(-75.08, -9.15) * mm, v(-73.91, -8.19) * mm, v(-72.17, -7.08) * mm, v(-70.2, -6.14) * mm, v(-68.5, -5.56) * mm, v(-66.99, -5.12) * mm, v(-65.36, -4.81) * mm, v(-62.94, -4.57) * mm, v(-58.71, -4.59) * mm, v(-56.5, -4.84) * mm, v(-53.7, -5.36) * mm, v(-51.14, -6.1) * mm, v(-48.97, -6.88) * mm, v(-46.46, -7.95) * mm, v(-43.67, -9.37) * mm, v(-41.9, -10.42) * mm, v(-40.56, -11.32) * mm, v(-40.5, -11.35) * mm, v(-39.89, -11.16) * mm, v(-38.65, -11) * mm, v(-36.56, -10.93) * mm, v(-34.8, -11) * mm, v(-32.47, -11.55) * mm, v(-31.62, -12.1) * mm, v(-31, -12.96) * mm, v(-30.8, -13.65) * mm, v(-30.88, -14.61) * mm, v(-31.26, -15.69) * mm, v(-31.72, -16.4) * mm, v(-32.4, -17.17) * mm, v(-33.22, -17.9) * mm, v(-33.49, -18.13) * mm, v(-33.28, -18.45) * mm, v(-32.73, -19.28) * mm, v(-32.05, -20.57) * mm, v(-31.62, -21.65) * mm], "startDerivative": vector(109.95, 88.6) * mm, "endDerivative": vector(58.12, -136.3) * mm});
            skFitSpline(sketch, "E45", {"points": [v(-31.62, -21.65) * mm, v(-31.25, -22.9) * mm, v(-31.03, -24.65) * mm, v(-31.1, -25.37) * mm, v(-31.33, -25.6) * mm, v(-31.7, -25.68) * mm, v(-32.02, -25.3) * mm, v(-32.05, -24.75) * mm, v(-32.08, -23.6) * mm, v(-32.51, -21.93) * mm, v(-33.08, -20.3) * mm, v(-34.11, -18.57) * mm, v(-34.13, -18.55) * mm, v(-34.77, -19.05) * mm, v(-35.54, -19.58) * mm, v(-36.98, -20.45) * mm, v(-38.63, -21.31) * mm, v(-40.53, -22.17) * mm, v(-43.03, -23.17) * mm, v(-45.7, -24.14) * mm, v(-49.99, -25.34) * mm, v(-52.47, -25.87) * mm, v(-55.56, -26.37) * mm, v(-58.1, -26.57) * mm, v(-59.15, -26.6) * mm, v(-60.81, -26.48) * mm, v(-60.84, -26.49) * mm, v(-61.3, -27.3) * mm, v(-62.18, -28.65) * mm, v(-62.9, -29.95) * mm, v(-63.42, -30.95) * mm, v(-64, -32.24) * mm, v(-64.42, -33.3) * mm, v(-64.9, -34.7) * mm, v(-65.23, -36.17) * mm, v(-65.5, -37.88) * mm, v(-65.53, -39.48) * mm, v(-65.4, -41.37) * mm, v(-64.98, -42.97) * mm, v(-64.63, -43.76) * mm, v(-63.78, -45.2) * mm, v(-63.06, -46) * mm, v(-62.01, -46.87) * mm, v(-60.66, -47.63) * mm, v(-58, -48.39) * mm, v(-56.66, -48.52) * mm, v(-55.04, -48.54) * mm, v(-53.16, -48.3) * mm, v(-51.08, -47.86) * mm, v(-48.18, -46.74) * mm, v(-45.6, -45.18) * mm, v(-43.53, -43.47) * mm, v(-41.54, -41.48) * mm, v(-40.01, -39.68) * mm, v(-38.77, -37.91) * mm, v(-37.6, -35.72) * mm, v(-36.7, -33.15) * mm, v(-36.52, -30.42) * mm, v(-36.85, -28.75) * mm, v(-37.71, -27.42) * mm, v(-38.89, -26.54) * mm, v(-40.29, -26.04) * mm, v(-41.49, -25.94) * mm, v(-42.82, -25.97) * mm, v(-44.56, -26.49) * mm, v(-46.37, -27.39) * mm, v(-48.1, -28.59) * mm, v(-49.58, -29.88) * mm, v(-51.13, -31.47) * mm, v(-52.27, -32.86) * mm, v(-52.88, -33.8) * mm, v(-53.48, -35.02) * mm, v(-53.83, -36.37) * mm, v(-53.88, -37.28) * mm, v(-53.82, -37.44) * mm, v(-53.65, -37.35) * mm], "startDerivative": vector(31.65, -93.9) * mm, "endDerivative": vector(42.22, 30.61) * mm});
            skFitSpline(sketch, "E46", {"points": [v(-64.74, -25.51) * mm, v(-63.3, -23.64) * mm, v(-62.38, -22.6) * mm, v(-61.25, -21.41) * mm, v(-60.07, -20.36) * mm, v(-59.06, -19.47) * mm, v(-57.24, -18.09) * mm, v(-55.47, -16.91) * mm, v(-52.97, -15.48) * mm, v(-51.63, -14.8) * mm, v(-49.66, -13.94) * mm, v(-48.02, -13.32) * mm, v(-45.97, -12.61) * mm, v(-44.65, -12.23) * mm, v(-41.77, -11.54) * mm, v(-41.58, -11.5) * mm, v(-41.94, -11.34) * mm, v(-43.94, -10.31) * mm, v(-45.89, -9.38) * mm, v(-48.12, -8.55) * mm, v(-51.2, -7.59) * mm, v(-55.13, -6.8) * mm, v(-56.5, -6.59) * mm, v(-59.27, -6.33) * mm, v(-61.23, -6.33) * mm, v(-63, -6.41) * mm, v(-65.18, -6.65) * mm, v(-67.31, -7.17) * mm, v(-69.04, -7.73) * mm, v(-70.4, -8.34) * mm, v(-71.72, -9.06) * mm, v(-73.22, -10) * mm, v(-74.32, -10.9) * mm, v(-75.61, -12.4) * mm, v(-76.27, -13.56) * mm, v(-76.65, -14.44) * mm, v(-76.8, -15.24) * mm, v(-76.88, -16.3) * mm, v(-76.85, -17.36) * mm, v(-76.56, -18.55) * mm, v(-76.14, -19.59) * mm, v(-75.45, -20.6) * mm, v(-74.87, -21.3) * mm, v(-73.98, -22.04) * mm, v(-72.81, -22.86) * mm, v(-71.62, -23.52) * mm, v(-70.27, -24.07) * mm, v(-67.85, -24.85) * mm, v(-64.82, -25.58) * mm, v(-64.76, -25.54) * mm, v(-64.74, -25.51) * mm]});
            skFitSpline(sketch, "E47", {"points": [v(-60.33, -25.82) * mm, v(-58.78, -23.94) * mm, v(-57.42, -22.44) * mm, v(-56.2, -21.23) * mm, v(-54.59, -19.73) * mm, v(-52.95, -18.47) * mm, v(-51.19, -17.16) * mm, v(-49.33, -15.95) * mm, v(-47.44, -14.85) * mm, v(-44.7, -13.56) * mm, v(-42.8, -12.88) * mm, v(-40.67, -12.15) * mm, v(-40.6, -12.14) * mm, v(-40.55, -12.16) * mm, v(-40.44, -12.26) * mm, v(-38.83, -13.42) * mm, v(-37.57, -14.54) * mm, v(-36.56, -15.54) * mm, v(-35.76, -16.35) * mm, v(-35.01, -17.2) * mm, v(-34.44, -17.97) * mm, v(-34.43, -17.99) * mm, v(-34.44, -18) * mm, v(-35.99, -19.01) * mm, v(-39.58, -20.98) * mm, v(-44.28, -22.78) * mm, v(-48.54, -24.1) * mm, v(-52.23, -24.97) * mm, v(-55.66, -25.53) * mm, v(-58.73, -25.86) * mm, v(-60.25, -25.88) * mm, v(-60.33, -25.87) * mm, v(-60.36, -25.87) * mm, v(-60.36, -25.86) * mm, v(-60.35, -25.85) * mm, v(-60.33, -25.82) * mm]});
            skLineSegment(sketch, "E48", {"start": v(-21.92, -16.62) * mm, "end": v(-40.11, -48.28) * mm});
            skFitSpline(sketch, "E49", {"points": [v(-40.11, -48.28) * mm, v(-39.33, -48.1) * mm, v(-38.13, -48) * mm, v(-36.91, -48.17) * mm, v(-36.57, -48.38) * mm], "startDerivative": vector(3.1, 0.77) * mm, "endDerivative": vector(1.6, -1.34) * mm});
            skLineSegment(sketch, "E50", {"start": v(-36.57, -48.38) * mm, "end": v(-32.15, -40.76) * mm});
            skFitSpline(sketch, "E51", {"points": [v(-32.15, -40.76) * mm, v(-30.56, -38.38) * mm, v(-28.86, -36.17) * mm, v(-26.78, -33.8) * mm, v(-25.14, -32.48) * mm, v(-24.1, -31.86) * mm, v(-23.74, -31.78) * mm, v(-23.23, -31.73) * mm, v(-22.74, -31.8) * mm, v(-22.37, -32.07) * mm, v(-22.2, -32.63) * mm, v(-22.31, -33.39) * mm, v(-22.85, -34.4) * mm, v(-24.98, -37.84) * mm, v(-27, -41) * mm, v(-27.57, -42.13) * mm, v(-27.92, -43.36) * mm, v(-28.06, -44.13) * mm, v(-28.02, -45.25) * mm, v(-27.84, -46.05) * mm, v(-27.55, -46.8) * mm, v(-27.06, -47.4) * mm, v(-26.56, -47.82) * mm, v(-25.94, -48.19) * mm, v(-25.03, -48.43) * mm, v(-24, -48.33) * mm, v(-22.53, -47.66) * mm, v(-20.68, -46.09) * mm, v(-18.47, -43.6) * mm, v(-16.98, -41.63) * mm, v(-16.68, -41.19) * mm, v(-16.66, -41.17) * mm, v(-16.64, -41.2) * mm, v(-16.85, -41.87) * mm, v(-16.9, -43.84) * mm, v(-16.66, -44.89) * mm, v(-16.07, -46.1) * mm, v(-15.1, -47.15) * mm, v(-14.5, -47.61) * mm, v(-13.45, -48.17) * mm, v(-12.41, -48.4) * mm, v(-11.45, -48.43) * mm, v(-10.25, -48.19) * mm, v(-7.7, -47.02) * mm, v(-6.27, -46.02) * mm, v(-4.65, -44.62) * mm, v(-2.6, -42.57) * mm, v(-1.05, -40.76) * mm, v(0.36, -38.96) * mm, v(1.99, -36.73) * mm, v(4.05, -34.02) * mm, v(5.68, -32.36) * mm, v(6.61, -31.77) * mm, v(6.94, -31.71) * mm, v(7.32, -31.85) * mm, v(7.53, -32.2) * mm, v(7.52, -32.88) * mm, v(7.18, -33.81) * mm, v(6.22, -35.88) * mm, v(5.26, -37.54) * mm, v(4.57, -38.68) * mm, v(3.45, -40.5) * mm, v(2.12, -42.67) * mm, v(-1.2, -48.1) * mm], "startDerivative": vector(69.12, 106.77) * mm, "endDerivative": vector(-109.16, -178.7) * mm});
            skFitSpline(sketch, "E52", {"points": [v(-1.2, -48.1) * mm, v(-0.4, -47.98) * mm, v(0.78, -47.92) * mm, v(1.81, -48.02) * mm, v(2.74, -48.1) * mm], "startDerivative": vector(3.3, 0.62) * mm, "endDerivative": vector(3.79, -0.3) * mm});
            skFitSpline(sketch, "E53", {"points": [v(2.74, -48.1) * mm, v(4.24, -45.58) * mm, v(5.84, -42.97) * mm, v(7.22, -40.96) * mm, v(8.23, -39.8) * mm, v(9.45, -38.62) * mm, v(9.63, -38.43) * mm, v(9.7, -38.4) * mm, v(9.7, -38.49) * mm, v(9.65, -38.82) * mm, v(9.45, -39.75) * mm, v(9.5, -41.04) * mm, v(9.97, -42.2) * mm, v(10.52, -42.7) * mm, v(11.37, -42.99) * mm, v(11.96, -43.02) * mm, v(12.81, -42.89) * mm, v(14.02, -42.35) * mm, v(15.42, -41.25) * mm, v(15.97, -40.67) * mm, v(16.12, -40.48) * mm, v(16.16, -40.47) * mm, v(16.12, -40.58) * mm, v(15.66, -41.33) * mm, v(15.15, -42.42) * mm, v(14.9, -43.07) * mm, v(14.53, -44.73) * mm, v(14.7, -45.71) * mm, v(15, -46.61) * mm, v(15.93, -47.66) * mm, v(16.46, -48) * mm, v(17.25, -48.33) * mm, v(18.05, -48.41) * mm, v(18.95, -48.24) * mm, v(19.91, -47.75) * mm, v(21.14, -46.94) * mm, v(22.45, -45.75) * mm, v(23.8, -44.31) * mm, v(24.91, -42.84) * mm, v(25.76, -41.73) * mm, v(25.8, -41.68) * mm, v(25.82, -41.7) * mm, v(25.81, -41.77) * mm, v(25.57, -42.17) * mm, v(24.66, -43.73) * mm, v(23.62, -45.5) * mm, v(22.9, -46.87) * mm, v(21.64, -49.14) * mm, v(20.62, -50.84) * mm, v(19.79, -52.3) * mm, v(18.47, -54.35) * mm, v(17.09, -56.2) * mm, v(15.6, -57.7) * mm, v(13.67, -59.41) * mm, v(10.96, -61.06) * mm, v(9.36, -61.67) * mm, v(7.24, -62.08) * mm, v(6, -62.06) * mm, v(4.97, -61.86) * mm, v(4.28, -61.73) * mm, v(3.85, -61.86) * mm, v(3.72, -62.3) * mm, v(4, -62.6) * mm, v(4.67, -62.84) * mm, v(5.48, -62.9) * mm, v(6.38, -62.92) * mm, v(7.8, -62.8) * mm, v(9.18, -62.54) * mm, v(10.79, -61.93) * mm, v(12.43, -61.2) * mm, v(13.89, -60.4) * mm, v(15.81, -59.04) * mm, v(17.34, -57.8) * mm, v(19.96, -55.35) * mm, v(22.15, -53.03) * mm, v(23.95, -50.85) * mm, v(25.47, -48.67) * mm, v(26.74, -46.7) * mm, v(28.15, -44.4) * mm, v(30, -41.04) * mm, v(32.19, -36.97) * mm, v(33.84, -33.62) * mm, v(34.72, -31.9) * mm, v(34.83, -31.7) * mm, v(34.94, -31.67) * mm, v(40.03, -31.66) * mm], "startDerivative": vector(83.46, 141.1) * mm, "endDerivative": vector(323.7, -11.15) * mm});
            skLineSegment(sketch, "E54", {"start": v(40.03, -31.66) * mm, "end": v(40.4, -31.05) * mm});
            skLineSegment(sketch, "E55", {"start": v(40.4, -31.05) * mm, "end": v(35.33, -31.1) * mm});
            skFitSpline(sketch, "E56", {"points": [v(35.33, -31.1) * mm, v(37.51, -29.7) * mm, v(40, -27.87) * mm, v(42.87, -25.5) * mm, v(44.4, -24.1) * mm, v(46.4, -21.83) * mm, v(47.45, -20.55) * mm, v(48.49, -18.64) * mm, v(48.89, -17.43) * mm, v(49.02, -16.56) * mm, v(48.84, -15.58) * mm, v(48.5, -15.1) * mm, v(47.86, -14.91) * mm, v(46.52, -15) * mm, v(45.12, -15.67) * mm, v(43.87, -16.44) * mm, v(42.53, -17.54) * mm, v(41.8, -18.15) * mm, v(37.52, -22.68) * mm, v(35.33, -25.44) * mm, v(33.67, -27.8) * mm, v(31.68, -31.1) * mm], "startDerivative": vector(40.46, 25.25) * mm, "endDerivative": vector(-30.7, -52.21) * mm});
            skLineSegment(sketch, "E57", {"start": v(31.68, -31.1) * mm, "end": v(28.45, -31.1) * mm});
            skLineSegment(sketch, "E58", {"start": v(28.45, -31.1) * mm, "end": v(28.12, -31.62) * mm});
            skLineSegment(sketch, "E59", {"start": v(28.12, -31.62) * mm, "end": v(31.35, -31.7) * mm});
            skLineSegment(sketch, "E60", {"start": v(31.35, -31.7) * mm, "end": v(27.46, -38.63) * mm});
            skFitSpline(sketch, "E61", {"points": [v(27.46, -38.63) * mm, v(26.66, -39.67) * mm, v(25.38, -41.38) * mm, v(24.08, -43.06) * mm, v(22.12, -45.24) * mm, v(20.54, -46.65) * mm, v(18.88, -47.66) * mm, v(18.2, -47.69) * mm, v(17.64, -47.57) * mm, v(17.22, -47.2) * mm, v(17.1, -46.42) * mm, v(17.16, -45.7) * mm, v(17.57, -44.57) * mm, v(18.5, -42.75) * mm, v(20.03, -40.26) * mm, v(25.52, -31.2) * mm], "startDerivative": vector(-13.18, -16.87) * mm, "endDerivative": vector(39.1, 65.17) * mm});
            skFitSpline(sketch, "E62", {"points": [v(25.52, -31.2) * mm, v(24.25, -31.47) * mm, v(22.7, -31.5) * mm, v(21.94, -31.36) * mm, v(21.55, -31.2) * mm], "startDerivative": vector(-4.12, -1.1) * mm, "endDerivative": vector(-2.2, 1.03) * mm});
            skFitSpline(sketch, "E63", {"points": [v(21.55, -31.2) * mm, v(17.47, -38.05) * mm, v(16.08, -39.7) * mm, v(14.63, -41.18) * mm, v(13.28, -42.01) * mm, v(11.99, -42.39) * mm, v(10.97, -42.1) * mm, v(10.31, -41.27) * mm, v(10.15, -39.7) * mm, v(10.38, -38.2) * mm, v(10.52, -37.73) * mm, v(11.12, -37.32) * mm, v(13.36, -35.92) * mm, v(15.31, -34.47) * mm, v(16.4, -33.43) * mm, v(16.94, -32.8) * mm, v(17.09, -32.4) * mm, v(17.16, -32.03) * mm, v(17.02, -31.5) * mm, v(16.6, -31.13) * mm, v(15.94, -31.04) * mm, v(15.23, -31.15) * mm, v(14.06, -31.82) * mm, v(13.17, -32.6) * mm, v(12.1, -33.86) * mm, v(10.77, -35.87) * mm, v(10.14, -37.2) * mm, v(9.79, -37.66) * mm, v(8.36, -38.94) * mm, v(7.64, -39.78) * mm, v(7.6, -39.81) * mm, v(7.59, -39.8) * mm, v(8.28, -38.78) * mm, v(8.9, -37.5) * mm, v(9.4, -36.33) * mm, v(9.73, -35.2) * mm, v(9.63, -32.99) * mm, v(9.28, -32.09) * mm, v(8.7, -31.44) * mm, v(7.99, -31.09) * mm, v(7.4, -31) * mm, v(6.66, -31.15) * mm, v(5.85, -31.56) * mm, v(5.12, -32.21) * mm, v(4.33, -32.96) * mm, v(3.2, -34.24) * mm, v(2.32, -35.27) * mm, v(1.38, -36.45) * mm, v(0.39, -37.77) * mm, v(-0.51, -38.96) * mm, v(-2.13, -41) * mm, v(-2.97, -41.94) * mm, v(-3.64, -42.73) * mm, v(-4.86, -43.95) * mm, v(-6.16, -45.07) * mm, v(-6.56, -45.36) * mm, v(-7.64, -46.17) * mm, v(-8.93, -46.93) * mm, v(-10.24, -47.39) * mm, v(-11.37, -47.6) * mm, v(-12.5, -47.6) * mm, v(-13.38, -47.28) * mm, v(-14.01, -46.65) * mm, v(-14.25, -45.98) * mm, v(-14.36, -45.04) * mm, v(-14.05, -43.57) * mm, v(-13.4, -41.86) * mm, v(-12.64, -40.5) * mm, v(-12.4, -40.03) * mm, v(-12.4, -40.02) * mm, v(-10.99, -39.8) * mm, v(-9.03, -39.33) * mm, v(-6.85, -38.76) * mm, v(-4.98, -38.13) * mm, v(-3.44, -37.5) * mm, v(-2.04, -36.77) * mm, v(-1.06, -35.9) * mm, v(-0.26, -34.8) * mm, v(-0.06, -34.2) * mm, v(0.03, -33.58) * mm, v(-0.06, -32.84) * mm, v(-0.34, -32.22) * mm, v(-0.89, -31.62) * mm, v(-1.52, -31.25) * mm, v(-2.04, -31.11) * mm, v(-2.98, -31) * mm, v(-4.24, -31.2) * mm, v(-5.43, -31.51) * mm, v(-6.45, -31.89) * mm, v(-8.23, -32.66) * mm, v(-9.95, -33.57) * mm, v(-11.45, -34.5) * mm, v(-14.06, -36.7) * mm, v(-15.81, -38.83) * mm, v(-16.17, -39.52) * mm, v(-16.9, -40.5) * mm, v(-18.1, -42.15) * mm, v(-20.17, -44.65) * mm, v(-21.32, -45.92) * mm, v(-22.29, -46.68) * mm, v(-23.31, -47.4) * mm, v(-24.14, -47.69) * mm, v(-24.73, -47.66) * mm, v(-25.24, -47.38) * mm, v(-25.46, -46.9) * mm, v(-25.47, -46.47) * mm, v(-25.23, -45.52) * mm, v(-24.64, -44.37) * mm, v(-24.24, -43.79) * mm, v(-23.25, -42.06) * mm, v(-22.46, -40.93) * mm, v(-21.4, -39.32) * mm, v(-20.8, -38.07) * mm, v(-20.28, -37.03) * mm, v(-19.94, -35.8) * mm, v(-19.86, -34.76) * mm, v(-20.02, -33.7) * mm, v(-20.44, -32.8) * mm, v(-20.97, -32.03) * mm, v(-21.63, -31.47) * mm, v(-22.44, -31.14) * mm, v(-23.2, -31.02) * mm, v(-24.06, -31.14) * mm, v(-25.36, -31.75) * mm, v(-26.77, -32.85) * mm, v(-28.07, -34.14) * mm, v(-29.25, -35.51) * mm, v(-29.95, -36.44) * mm, v(-31.14, -38.1) * mm, v(-31.67, -38.93) * mm, v(-31.7, -38.98) * mm, v(-31.72, -39) * mm, v(-31.73, -38.98) * mm, v(-29.9, -35.94) * mm, v(-28.74, -34.08) * mm, v(-26.9, -31.08) * mm, v(-26.07, -29.87) * mm, v(-24.83, -27.74) * mm, v(-23.65, -25.88) * mm, v(-21.97, -23.14) * mm, v(-21.3, -22.04) * mm, v(-18.31, -17.22) * mm, v(-17.9, -16.5) * mm], "startDerivative": vector(-257.4, -454.67) * mm, "endDerivative": vector(45.34, 84.47) * mm});
            skFitSpline(sketch, "E64", {"points": [v(-21.92, -16.62) * mm, v(-21.13, -16.86) * mm, v(-19.6, -16.86) * mm, v(-18.59, -16.67) * mm, v(-17.9, -16.5) * mm], "startDerivative": vector(3.08, -1.26) * mm, "endDerivative": vector(3.2, 0.86) * mm});
            skFitSpline(sketch, "E65", {"points": [v(-12.16, -39.5) * mm, v(-10.62, -37.45) * mm, v(-9.62, -36.31) * mm, v(-7.83, -34.5) * mm, v(-6.28, -33.17) * mm, v(-4.56, -32.1) * mm, v(-3.28, -31.67) * mm, v(-2.77, -31.63) * mm, v(-2.32, -31.68) * mm, v(-2.07, -31.83) * mm, v(-1.93, -32.03) * mm, v(-1.84, -32.26) * mm, v(-1.81, -32.62) * mm, v(-1.94, -33.15) * mm, v(-2.23, -33.76) * mm, v(-2.76, -34.5) * mm, v(-3.6, -35.37) * mm, v(-4.22, -35.86) * mm, v(-5.19, -36.55) * mm, v(-6.52, -37.34) * mm, v(-7.74, -37.96) * mm, v(-8.8, -38.39) * mm, v(-9.87, -38.8) * mm, v(-11.2, -39.25) * mm, v(-11.95, -39.48) * mm], "startDerivative": vector(24.92, 34) * mm, "endDerivative": vector(-18.62, -5.6) * mm});
            skLineSegment(sketch, "E66", {"start": v(-11.95, -39.48) * mm, "end": v(-12.16, -39.5) * mm});
            skFitSpline(sketch, "E67", {"points": [v(35.43, -30.45) * mm, v(39.13, -27.56) * mm, v(41.52, -25.46) * mm, v(44.58, -22.38) * mm, v(46.18, -20.53) * mm, v(47.83, -18.16) * mm, v(48.42, -16.64) * mm, v(48.33, -15.8) * mm, v(47.9, -15.48) * mm, v(47.03, -15.45) * mm, v(45.98, -16.02) * mm, v(44.48, -17.12) * mm, v(43.13, -18.5) * mm, v(41.37, -20.65) * mm, v(40.16, -22.44) * mm, v(39.17, -24.04) * mm, v(38.27, -25.55) * mm, v(37, -27.77) * mm, v(35.81, -29.79) * mm, v(35.43, -30.45) * mm], "startDerivative": vector(49.17, 37.93) * mm, "endDerivative": vector(-10.07, -17.5) * mm});
            skLineSegment(sketch, "E68", {"start": v(35.43, -30.45) * mm, "end": v(35.43, -30.45) * mm});
            skFitSpline(sketch, "E69", {"points": [v(24.23, -25.5) * mm, v(25.08, -24.71) * mm, v(25.92, -24.24) * mm, v(26.58, -24.13) * mm, v(27.33, -24.32) * mm, v(27.78, -24.64) * mm, v(28.03, -25.52) * mm, v(27.73, -26.8) * mm, v(26.98, -27.73) * mm, v(25.92, -28.44) * mm, v(25.03, -28.57) * mm, v(24.34, -28.44) * mm, v(23.83, -28.06) * mm, v(23.6, -27.53) * mm, v(23.6, -26.8) * mm, v(23.85, -26) * mm, v(24.23, -25.5) * mm]});
            skFitSpline(sketch, "E70", {"points": [v(-39.7, -12) * mm, v(-37.81, -13.35) * mm, v(-36.9, -14.17) * mm, v(-35.25, -15.83) * mm, v(-34.24, -17.1) * mm, v(-33.89, -17.63) * mm], "startDerivative": vector(8.7, -5.87) * mm, "endDerivative": vector(2.41, -3.8) * mm});
            skFitSpline(sketch, "E71", {"points": [v(-39.7, -12) * mm, v(-37.9, -11.71) * mm, v(-35.7, -11.58) * mm, v(-34.2, -11.77) * mm, v(-33.37, -11.9) * mm, v(-32.38, -12.38) * mm, v(-31.8, -12.88) * mm, v(-31.5, -13.73) * mm, v(-31.57, -14.83) * mm, v(-32.36, -16.01) * mm, v(-33.33, -17.15) * mm, v(-33.89, -17.63) * mm], "startDerivative": vector(15.7, 2.79) * mm, "endDerivative": vector(-7.46, -5.96) * mm});
            skFitSpline(sketch, "E72", {"points": [v(7.99, -19.92) * mm, v(7.18, -20.9) * mm, v(6.16, -21.93) * mm, v(4.04, -23.74) * mm, v(2, -25.1) * mm, v(-0.61, -26.6) * mm, v(-2.58, -27.6) * mm, v(-2.72, -27.71) * mm, v(-2.72, -27.77) * mm, v(-2.56, -27.82) * mm, v(-2.12, -27.8) * mm, v(1.34, -26.5) * mm, v(3.18, -25.7) * mm, v(6.04, -24.28) * mm, v(7.78, -23.21) * mm, v(9.05, -22.33) * mm, v(9.28, -22.17) * mm, v(9.32, -22.09) * mm, v(9.3, -21.93) * mm, v(8.09, -20.06) * mm], "startDerivative": vector(-14.9, -18.67) * mm, "endDerivative": vector(-23.48, 33.53) * mm});
            skLineSegment(sketch, "E73", {"start": v(8.09, -20.06) * mm, "end": v(7.99, -19.92) * mm});
            skLineSegment(sketch, "E74", {"start": v(25.03, -28.31) * mm, "end": v(23.98, -31.84) * mm});
            skLineSegment(sketch, "E75", {"start": v(23.98, -31.84) * mm, "end": v(24.96, -31.7) * mm});
            skLineSegment(sketch, "E76", {"start": v(24.96, -31.7) * mm, "end": v(26, -28.06) * mm});
            skLineSegment(sketch, "E77", {"start": v(26, -28.06) * mm, "end": v(25.03, -28.31) * mm});
            skLineSegment(sketch, "E78", {"start": v(-2.32, -27.67) * mm, "end": v(-1.29, -27.46) * mm});
            skLineSegment(sketch, "E79", {"start": v(-1.29, -27.46) * mm, "end": v(-2, -31.3) * mm});
            skLineSegment(sketch, "E80", {"start": v(-2, -31.3) * mm, "end": v(-3.03, -31.27) * mm});
            skLineSegment(sketch, "E81", {"start": v(-3.03, -31.27) * mm, "end": v(-2.32, -27.67) * mm});
            skFitSpline(sketch, "E82", {"points": [v(-44.99, -45.71) * mm, v(-41.34, -45.05) * mm, v(-38.33, -43.69) * mm, v(-36.2, -42.19) * mm, v(-35.56, -41.58) * mm, v(-35.41, -41.78) * mm, v(-35.85, -42.82) * mm, v(-37.44, -44.06) * mm, v(-40.07, -45.22) * mm, v(-44.06, -46.12) * mm, v(-45.28, -46.25) * mm], "startDerivative": vector(27.46, 3.5) * mm, "endDerivative": vector(-12.83, -0.97) * mm});
            skLineSegment(sketch, "E83", {"start": v(-45.28, -46.25) * mm, "end": v(-45.61, -45.9) * mm});
            skLineSegment(sketch, "E84", {"start": v(-45.61, -45.9) * mm, "end": v(-44.99, -45.71) * mm});
            skSolve(sketch);
        }
        {
            var Q0;
            {var subQ0=sQuery(id+"F0.wireOp",EDGE,"E45");Q0=makeQuery(id+"F0.imprint","IMPRINT",FACE,{"disambiguationData":[TD([[makeQuery(id+"F0.imprint","IMPRINT",EDGE,{"derivedFrom":subQ0}),-1.0]])]});}
            var Q1;
            {var subQ0=sQuery(id+"F0.wireOp",EDGE,"E83");Q1=makeQuery(id+"F0.imprint","IMPRINT",FACE,{"disambiguationData":[TD([[makeQuery(id+"F0.imprint","IMPRINT",EDGE,{"derivedFrom":subQ0}),-1.0]])]});}
            var Q2;
            {var subQ0=sQuery(id+"F0.wireOp",EDGE,"E82");var subQ4=sQuery(id+"F0.wireOp",EDGE,"E48");var subQ5=makeQuery(id+"F0.imprint","INTERSECT",VERTEX,{"disambiguationData":[OD(0.0)],"derivedFrom":[subQ4,subQ0]});Q2=makeQuery(id+"F0.imprint","IMPRINT",FACE,{"disambiguationData":[TD([[makeQuery(id+"F0.imprint","IMPRINT",EDGE,{"disambiguationData":[TD([[subQ5,-1.0]])],"derivedFrom":subQ4}),-1.0]])]});}
            var Q3;
            {var subQ0=sQuery(id+"F0.wireOp",EDGE,"E82");var subQ1=sQuery(id+"F0.wireOp",EDGE,"E48");var subQ2=makeQuery(id+"F0.imprint","INTERSECT",VERTEX,{"disambiguationData":[OD(0.0)],"derivedFrom":[subQ1,subQ0]});Q3=makeQuery(id+"F0.imprint","IMPRINT",FACE,{"disambiguationData":[TD([[makeQuery(id+"F0.imprint","IMPRINT",EDGE,{"disambiguationData":[TD([[subQ2,-1.0]])],"derivedFrom":subQ1}),1.0]])]});}
            var Q4;
            {var subQ13=sQuery(id+"F0.wireOp",EDGE,"E49");Q4=makeQuery(id+"F0.imprint","IMPRINT",FACE,{"disambiguationData":[TD([[makeQuery(id+"F0.imprint","IMPRINT",EDGE,{"derivedFrom":subQ13}),1.0]])]});}
            var Q5;
            {var subQ5=sQuery(id+"F0.wireOp",EDGE,"E80");Q5=makeQuery(id+"F0.imprint","IMPRINT",FACE,{"disambiguationData":[TD([[makeQuery(id+"F0.imprint","IMPRINT",EDGE,{"derivedFrom":subQ5}),-1.0]])]});}
            var Q6;
            {var subQ0=sQuery(id+"F0.wireOp",EDGE,"E79");var subQ1=sQuery(id+"F0.wireOp",EDGE,"E63");var subQ2=makeQuery(id+"F0.imprint","INTERSECT",VERTEX,{"derivedFrom":[subQ1,subQ0]});Q6=makeQuery(id+"F0.imprint","IMPRINT",FACE,{"disambiguationData":[TD([[makeQuery(id+"F0.imprint","IMPRINT",EDGE,{"disambiguationData":[TD([[subQ2,-1.0]])],"derivedFrom":subQ1}),-1.0]])]});}
            var Q7;
            {var subQ0=sQuery(id+"F0.wireOp",EDGE,"E73");Q7=makeQuery(id+"F0.imprint","IMPRINT",FACE,{"disambiguationData":[TD([[makeQuery(id+"F0.imprint","IMPRINT",EDGE,{"derivedFrom":subQ0}),1.0]])]});}
            var Q8;
            {var subQ5=sQuery(id+"F0.wireOp",EDGE,"E78");Q8=makeQuery(id+"F0.imprint","IMPRINT",FACE,{"disambiguationData":[TD([[makeQuery(id+"F0.imprint","IMPRINT",EDGE,{"derivedFrom":subQ5}),-1.0]])]});}
            var Q9;
            {var subQ5=sQuery(id+"F0.wireOp",EDGE,"E77");Q9=makeQuery(id+"F0.imprint","IMPRINT",FACE,{"disambiguationData":[TD([[makeQuery(id+"F0.imprint","IMPRINT",EDGE,{"derivedFrom":subQ5}),1.0]])]});}
            var Q10;
            {var subQ5=sQuery(id+"F0.wireOp",EDGE,"E75");Q10=makeQuery(id+"F0.imprint","IMPRINT",FACE,{"disambiguationData":[TD([[makeQuery(id+"F0.imprint","IMPRINT",EDGE,{"derivedFrom":subQ5}),1.0]])]});}
            var Q11;
            {var subQ0=sQuery(id+"F0.wireOp",EDGE,"E76");var subQ1=sQuery(id+"F0.wireOp",EDGE,"E62");var subQ2=makeQuery(id+"F0.imprint","INTERSECT",VERTEX,{"derivedFrom":[subQ1,subQ0]});Q11=makeQuery(id+"F0.imprint","IMPRINT",FACE,{"disambiguationData":[TD([[makeQuery(id+"F0.imprint","IMPRINT",EDGE,{"disambiguationData":[TD([[subQ2,-1.0]])],"derivedFrom":subQ1}),-1.0]])]});}
            var Q12;
            {var subQ5=sQuery(id+"F0.wireOp",EDGE,"E77");Q12=makeQuery(id+"F0.imprint","IMPRINT",FACE,{"disambiguationData":[TD([[makeQuery(id+"F0.imprint","IMPRINT",EDGE,{"derivedFrom":subQ5}),-1.0]])]});}
            var Q13;
            Q13=makeQuery(id+"F0.imprint","IMPRINT",FACE,{"disambiguationData":[TD([[makeQuery(id+"F0.imprint","IMPRINT",EDGE,{"derivedFrom":sQuery(id+"F0.wireOp",EDGE,"E43")}),1.0]])]});
            var Q14;
            {var subQ0=sQuery(id+"F0.wireOp",EDGE,"E2");var subQ1=sQuery(id+"F0.wireOp",EDGE,"E1");var subQ2=makeQuery(id+"F0.imprint","INTERSECT",VERTEX,{"disambiguationData":[OD(0.0)],"derivedFrom":[subQ1,subQ0]});Q14=makeQuery(id+"F0.imprint","IMPRINT",FACE,{"disambiguationData":[TD([[makeQuery(id+"F0.imprint","IMPRINT",EDGE,{"disambiguationData":[TD([[subQ2,1.0]])],"derivedFrom":subQ1}),-1.0]])]});}
            var Q15;
            {var subQ0=sQuery(id+"F0.wireOp",EDGE,"E2");var subQ1=sQuery(id+"F0.wireOp",EDGE,"E1");var subQ2=makeQuery(id+"F0.imprint","INTERSECT",VERTEX,{"disambiguationData":[OD(0.0)],"derivedFrom":[subQ1,subQ0]});Q15=makeQuery(id+"F0.imprint","IMPRINT",FACE,{"disambiguationData":[TD([[makeQuery(id+"F0.imprint","IMPRINT",EDGE,{"disambiguationData":[TD([[subQ2,-1.0]])],"derivedFrom":subQ1}),-1.0]])]});}
            var Q16;
            {var subQ9=sQuery(id+"F0.wireOp",EDGE,"E41");Q16=makeQuery(id+"F0.imprint","IMPRINT",FACE,{"disambiguationData":[TD([[makeQuery(id+"F0.imprint","IMPRINT",EDGE,{"derivedFrom":subQ9}),-1.0]])]});}
            var Q17;
            {var subQ0=sQuery(id+"F0.wireOp",EDGE,"E3");var subQ1=sQuery(id+"F0.wireOp",EDGE,"E2");var subQ2=makeQuery(id+"F0.imprint","INTERSECT",VERTEX,{"disambiguationData":[OD(0.0)],"derivedFrom":[subQ1,subQ0]});Q17=makeQuery(id+"F0.imprint","IMPRINT",FACE,{"disambiguationData":[TD([[makeQuery(id+"F0.imprint","IMPRINT",EDGE,{"disambiguationData":[TD([[subQ2,1.0]])],"derivedFrom":subQ1}),1.0]])]});}
            var Q18;
            {var subQ0=sQuery(id+"F0.wireOp",EDGE,"E4");Q18=makeQuery(id+"F0.imprint","IMPRINT",FACE,{"disambiguationData":[TD([[makeQuery(id+"F0.imprint","IMPRINT",EDGE,{"derivedFrom":subQ0}),-1.0]])]});}
            var Q19;
            {var subQ5=sQuery(id+"F0.wireOp",EDGE,"E41");Q19=makeQuery(id+"F0.imprint","IMPRINT",FACE,{"disambiguationData":[TD([[makeQuery(id+"F0.imprint","IMPRINT",EDGE,{"derivedFrom":subQ5}),1.0]])]});}
            var Q20;
            {var subQ5=sQuery(id+"F0.wireOp",EDGE,"E39");Q20=makeQuery(id+"F0.imprint","IMPRINT",FACE,{"disambiguationData":[TD([[makeQuery(id+"F0.imprint","IMPRINT",EDGE,{"derivedFrom":subQ5}),1.0]])]});}
            extrude(context, id + "F1", {"entities" : qUnion([Q0, Q1, Q2, Q3, Q4, Q5, Q6, Q7, Q8, Q9, Q10, Q11, Q12, Q13, Q14, Q15, Q16, Q17, Q18, Q19, Q20]), "depth" : 5 * mm, "offsetDistance" : 25 * mm});
        }
        {
            var Q0;
            Q0=qCreatedBy(makeId("Top.planeOp"),FACE);
            var sketch = newSketch(context, id + "F2", { "sketchPlane" : qUnion([Q0])});
            skLineSegment(sketch, "E85", {"start": v(0, 5) * mm, "end": v(30, 5) * mm});
            skLineSegment(sketch, "E86", {"start": v(30, 5) * mm, "end": v(30, 0) * mm});
            skLineSegment(sketch, "E87", {"start": v(30, 0) * mm, "end": v(2.5, 0) * mm});
            skLineSegment(sketch, "E88", {"start": v(2.5, 0) * mm, "end": v(2.5, -170) * mm});
            skLineSegment(sketch, "E89", {"start": v(2.5, -170) * mm, "end": v(0, -184.22) * mm});
            skLineSegment(sketch, "E90.MirrorCS", {"start": v(0, 5) * mm, "end": v(-30, 5) * mm});
            skLineSegment(sketch, "E91.MirrorCS", {"start": v(-30, 5) * mm, "end": v(-30, 0) * mm});
            skLineSegment(sketch, "E92.MirrorCS", {"start": v(-30, 0) * mm, "end": v(-2.5, 0) * mm});
            skLineSegment(sketch, "E93.MirrorCS", {"start": v(-2.5, -170) * mm, "end": v(0, -184.22) * mm});
            skLineSegment(sketch, "E94.MirrorCS", {"start": v(-2.5, 0) * mm, "end": v(-2.5, -170) * mm});
            skSolve(sketch);
        }
        {
            var Q0;
            Q0 = qSketchRegion(id + "F2", true);
            extrude(context, id + "F3", {"entities" : qUnion([Q0]), "depth" : 2.5 * mm, "offsetDistance" : 25 * mm});
        }
    });
